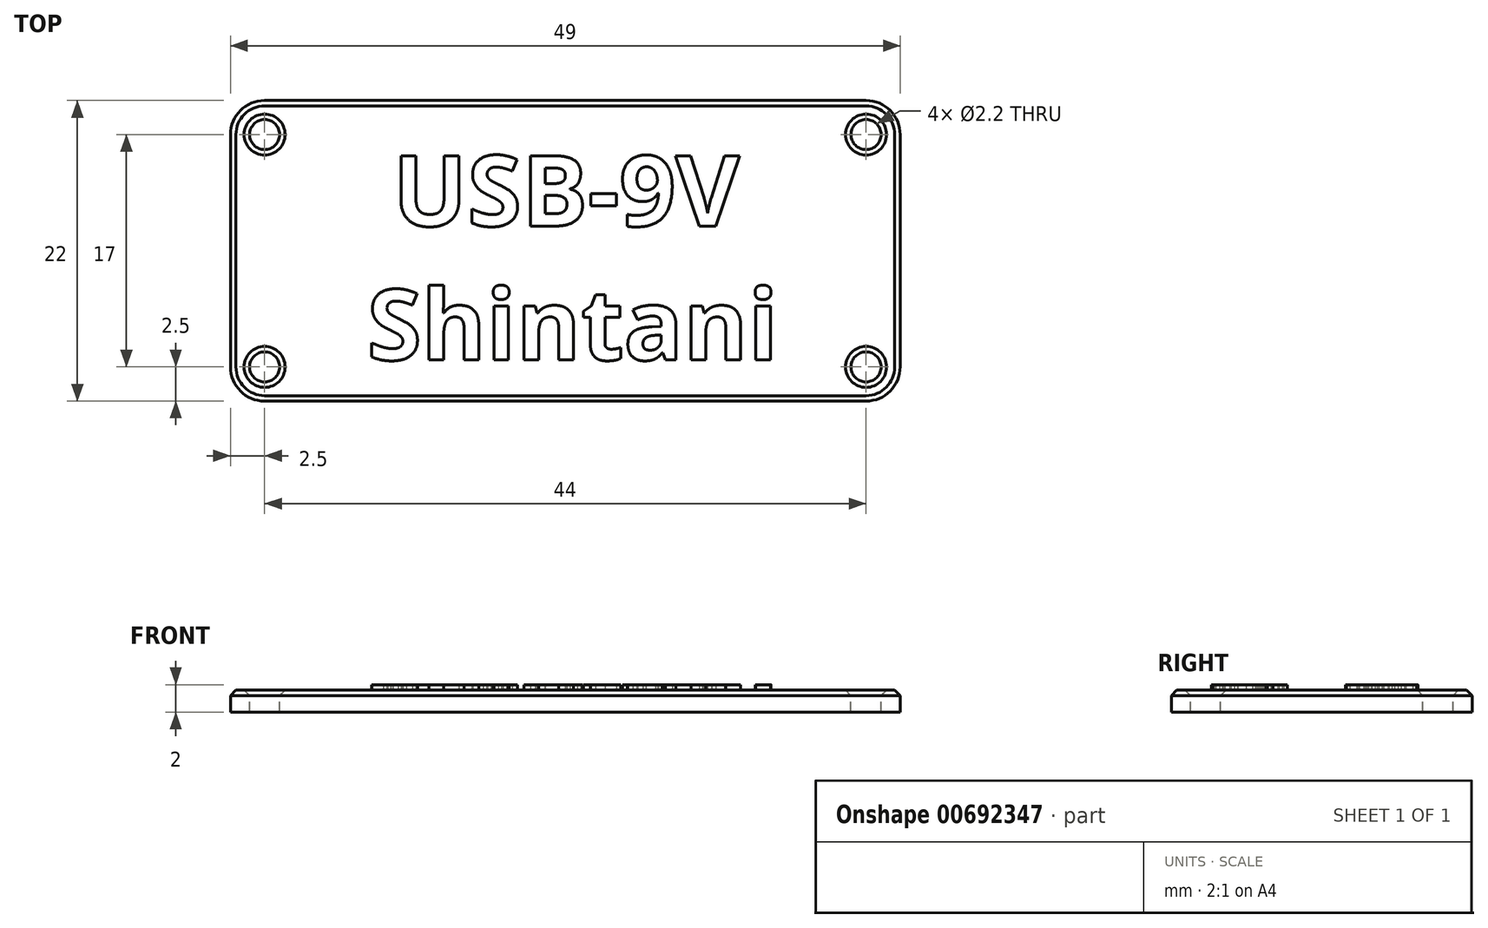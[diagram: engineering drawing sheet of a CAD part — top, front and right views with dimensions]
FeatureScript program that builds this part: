
annotation { "Feature Type Name" : "Feature", "Feature Type Description" : "" }
export const myFeature = defineFeature(function(context is Context, id is Id, definition is map)
    precondition{}
    {
        {
            var Q0;
            Q0=qCreatedBy(makeId("Top.planeOp"),FACE);
            var sketch = newSketch(context, id + "F0", { "sketchPlane" : qUnion([Q0])});
            skLineSegment(sketch, "E0.0", {"start": v(47, 20) * mm, "end": v(47, -2) * mm});
            skLineSegment(sketch, "E0.1", {"start": v(-2, 20) * mm, "end": v(47, 20) * mm});
            skLineSegment(sketch, "E0.2", {"start": v(-2, 20) * mm, "end": v(-2, -2) * mm});
            skLineSegment(sketch, "E0.3", {"start": v(-2, -2) * mm, "end": v(47, -2) * mm});
            skSolve(sketch);
        }
        {
            var Q0;
            Q0=qSketchRegion(id+"F0",true);
            extrude(context, id + "F1", {"entities" : qUnion([Q0]), "depth" : 1.6 * mm, "offsetDistance" : 25 * mm});
        }
        {
            var Q0;
            Q0=makeQuery(id+"FjB9nhuWzvWTUWx_1.boolean.opBoolean","MERGE",EDGE,{"derivedFrom":[makeQuery(id+"F1.opExtrude","SWEPT_EDGE",EDGE,{"disambiguationData":[OSD([sQuery(id+"F0.wireOp",EDGE,"E0.0"),sQuery(id+"F0.wireOp",EDGE,"E0.3")])]}),makeQuery(id+"FjB9nhuWzvWTUWx_1.opExtrude","SWEPT_EDGE",EDGE,{"disambiguationData":[OSD([sQuery(id+"FeVB2MOxy9sguIm_1.wireOp",EDGE,"0016a365-dab3-4718-a8a0-e545771e888a.1"),sQuery(id+"FeVB2MOxy9sguIm_1.wireOp",EDGE,"0016a365-dab3-4718-a8a0-e545771e888a.2")])]})]});
            var Q1;
            Q1=makeQuery(id+"FjB9nhuWzvWTUWx_1.boolean.opBoolean","MERGE",EDGE,{"derivedFrom":[makeQuery(id+"F1.opExtrude","SWEPT_EDGE",EDGE,{"disambiguationData":[OSD([sQuery(id+"F0.wireOp",EDGE,"E0.0"),sQuery(id+"F0.wireOp",EDGE,"E0.1")])]}),makeQuery(id+"FjB9nhuWzvWTUWx_1.opExtrude","SWEPT_EDGE",EDGE,{"disambiguationData":[OSD([sQuery(id+"FeVB2MOxy9sguIm_1.wireOp",EDGE,"804fd0ae-9b6a-4732-8e45-86920334032a.0"),sQuery(id+"FeVB2MOxy9sguIm_1.wireOp",EDGE,"0016a365-dab3-4718-a8a0-e545771e888a.2")])]})]});
            var Q2;
            Q2=makeQuery(id+"FjB9nhuWzvWTUWx_1.boolean.opBoolean","MERGE",EDGE,{"derivedFrom":[makeQuery(id+"F1.opExtrude","SWEPT_EDGE",EDGE,{"disambiguationData":[OSD([sQuery(id+"F0.wireOp",EDGE,"E0.1"),sQuery(id+"F0.wireOp",EDGE,"E0.2")])]}),makeQuery(id+"FjB9nhuWzvWTUWx_1.opExtrude","SWEPT_EDGE",EDGE,{"disambiguationData":[OSD([sQuery(id+"FeVB2MOxy9sguIm_1.wireOp",EDGE,"804fd0ae-9b6a-4732-8e45-86920334032a.0"),sQuery(id+"FeVB2MOxy9sguIm_1.wireOp",EDGE,"0016a365-dab3-4718-a8a0-e545771e888a.0")])]})]});
            var Q3;
            Q3=makeQuery(id+"FjB9nhuWzvWTUWx_1.boolean.opBoolean","MERGE",EDGE,{"derivedFrom":[makeQuery(id+"F1.opExtrude","SWEPT_EDGE",EDGE,{"disambiguationData":[OSD([sQuery(id+"F0.wireOp",EDGE,"E0.2"),sQuery(id+"F0.wireOp",EDGE,"E0.3")])]}),makeQuery(id+"FjB9nhuWzvWTUWx_1.opExtrude","SWEPT_EDGE",EDGE,{"disambiguationData":[OSD([sQuery(id+"FeVB2MOxy9sguIm_1.wireOp",EDGE,"0016a365-dab3-4718-a8a0-e545771e888a.0"),sQuery(id+"FeVB2MOxy9sguIm_1.wireOp",EDGE,"0016a365-dab3-4718-a8a0-e545771e888a.1")])]})]});
            fillet(context, id + "F2", {"entities" : qUnion([Q0, Q1, Q2, Q3]), "radius" : 2.5 * mm, "tangentPropagation" : true, "allowEdgeOverflow" : false});
        }
        {
            var Q0;
            Q0=makeQuery(id+"F1.opExtrude","CAP_FACE",FACE,{"disambiguationData":[OSD([sQuery(id+"F0.wireOp",EDGE,"E0.0"),sQuery(id+"F0.wireOp",EDGE,"E0.1"),sQuery(id+"F0.wireOp",EDGE,"E0.2"),sQuery(id+"F0.wireOp",EDGE,"E0.3")])],"isStart":false});
            var sketch = newSketch(context, id + "F3", { "sketchPlane" : qUnion([Q0])});
            skPoint(sketch, "E1", {"position": v(0.5, 17.5) * mm});
            skPoint(sketch, "E2", {"position": v(44.5, 17.5) * mm});
            skPoint(sketch, "E3", {"position": v(44.5, 0.5) * mm});
            skPoint(sketch, "E4", {"position": v(0.5, 0.5) * mm});
            skSolve(sketch);
        }
        {
            var Q0;
            Q0=sQuery(id+"F3.wireOp",VERTEX,"E3");
            var Q1;
            Q1=sQuery(id+"F3.wireOp",VERTEX,"E2");
            var Q2;
            Q2=sQuery(id+"F3.wireOp",VERTEX,"E1");
            var Q3;
            Q3=sQuery(id+"F3.wireOp",VERTEX,"E4");
            var Q4;
            Q4=makeQuery(id+"F1.opExtrude","SWEPT_BODY",BODY,{"disambiguationData":[OSD([sQuery(id+"F0.wireOp",EDGE,"E0.0"),sQuery(id+"F0.wireOp",EDGE,"E0.1"),sQuery(id+"F0.wireOp",EDGE,"E0.2"),sQuery(id+"F0.wireOp",EDGE,"E0.3")])]});
            hole(context, id + "F4", {"style" : HoleStyle.SIMPLE, "endStyle" : HoleEndStyle.THROUGH, "holeDiameter" : 2.2 * mm, "majorDiameter" : 5 * mm, "isTappedThrough" : true, "tappedDepth" : 12 * mm, "tapClearance" : 3, "locations" : qUnion([Q0, Q1, Q2, Q3]), "scope" : qUnion([Q4])});
        }
        {
            var Q0;
            Q0=makeQuery(id+"F1.opExtrude","CAP_FACE",FACE,{"disambiguationData":[OSD([sQuery(id+"F0.wireOp",EDGE,"E0.0"),sQuery(id+"F0.wireOp",EDGE,"E0.1"),sQuery(id+"F0.wireOp",EDGE,"E0.2"),sQuery(id+"F0.wireOp",EDGE,"E0.3")])],"isStart":false});
            chamfer(context, id + "F5", {"entities" : qUnion([Q0]), "width" : 0.4 * mm, "tangentPropagation" : true});
        }
        {
            var Q0;
            Q0=makeQuery(id+"F1.opExtrude","CAP_FACE",FACE,{"disambiguationData":[OSD([sQuery(id+"F0.wireOp",EDGE,"E0.0"),sQuery(id+"F0.wireOp",EDGE,"E0.1"),sQuery(id+"F0.wireOp",EDGE,"E0.2"),sQuery(id+"F0.wireOp",EDGE,"E0.3")])],"isStart":false});
            var sketch = newSketch(context, id + "F6", { "sketchPlane" : qUnion([Q0])});
            skText(sketch, "E5", { "text": " USB-9V\nShintani", "fontName": "OpenSans-Bold.ttf"});
            const initialGuessF6  = {"E5": [0.008, 0.01081, 1, 0, 0.00519]};
            skSetInitialGuess(sketch, initialGuessF6);
            skSolve(sketch);
        }
        {
            var Q0;
            Q0 = qSketchRegion(id + "F6", true);
            extrude(context, id + "F7", {"entities" : qUnion([Q0]), "operationType" : NewBodyOperationType.ADD, "depth" : 0.4 * mm, "offsetDistance" : 25 * mm});
        }
    });
